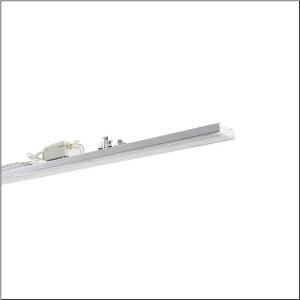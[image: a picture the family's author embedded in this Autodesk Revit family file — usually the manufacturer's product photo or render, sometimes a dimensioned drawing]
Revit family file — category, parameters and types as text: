
# Revit family: licross_11_recessed_mo_51te11cn49xg
name_source: partatom
category: Lighting Fixtures
units: mm (PartAtom-declared; Revit-internal decimal feet)

## family parameters
Cut with Voids When Loaded = No
Host = Face
Light Source = No
Part Type = Normal
Room Calculation Point = No
Round Connector Dimension = Use Diameter
Shared = No

## types (1)
- --- (1 x LED, 9160 lm, 49.3 W, 4000K)
    Apparent Load = 49 VA
    CIE Flux Codes = 89 96 99 100 100
    Color Rendering = 80
    Color Temperature = 4000K
    Default Elevation = 1800 mm
    Description = Licross 11 Recessed MO, luminaire insert, of sheet steel, galvanised, coil coated, white, length: 1.500mm, width: 66mm, height: 67mm, LED rated luminous flux: 9.060lm, light colour: 840, SDCM (Standard Deviation of Colour Matching)MacAdam ≤ 2 SDCM (initial), control gear: ON/OFF Multilumen, CLOi, with plug, 3-pole, with phase selection, mains connection: 220..240V, AC, 50/60Hz, start of lifetime: 49W, end of service life: 55W, internal wiring halogen-free, primary light control with lens, of plastic, primary optical cover: cover, of PMMA, light emission: direct distribution, primary light characteristic: symmetric, protection rating (complete): IP54, insulation class (complete): insulation class I (protective earthing), certification: CE, ENEC, VDE, UKCA, protection symbol: D if used in an environment with non-conductive dust loads with corresponding accessories, impact resistance: IK06, permissible ambient temperature for indoor applications: -35..+40°C, corresponds to IFS (International Featured Standards) requirements for safety and quality in the food industry, reducing of maximum allowable ambient temperature of 5°C with ceiling mounting, LABS conformity tested according to VDMA 24364:2018-05, The light source and the operating device comply with the requirements of the Ecodesign Regulation (EU) 2019/2020 and are replaceable in accordance with this regulation, packaging unit: 1 piece
    Height = 58 mm
    Lamp = 1 x LED
    Lamp Light Flux = 9160 lm
    Lamp Power = 49.3 W
    Lamp count = 1
    Length = 1500 mm
    Luminous efficacy = 186 lm/W
    Manufacturer = Siteco
    ModVariant = No
    Model = 51TE11CN49XG
    Mounting Place = Ceiling
    Mounting Type = Pendant
    Number of Poles = 1
    OnlyDefault = Yes
    Power Factor = 1
    Product Name = Licross 11 Recessed MO
    Product group = luminaire insert | ceiling pendant
    ProductGroupID = 901
    Protection Class = Protection class I
    Protection Degree = IP 54
    RLX_Detail_Level = 1
    RLX_Emergency_Light_Flux = 0 lm
    RLX_Emergency_Type = 0
    RLX_Emergency_Type_DB = No
    RlxData = <blob elided: 22553 chars, md5=ca98b535>
    Socket = socket
    Standby Power = 0 W
    System Light Flux = 9160 lm
    System Power = 49 W
    Type Comments = factory setting: luminous flux: 100 % | (A | C | E) | 113 mA
    Type Image = l_1296930.jpg
    URL = http://relux.com
    VarID = @adj_001379
    Voltage = 0 V
    Weight = 0.00 kg
    Width = 66 mm

## geometry (parser evidence)
native form markers: Blend x4, Sweep x11
no freeform markers — native parametric forms only
